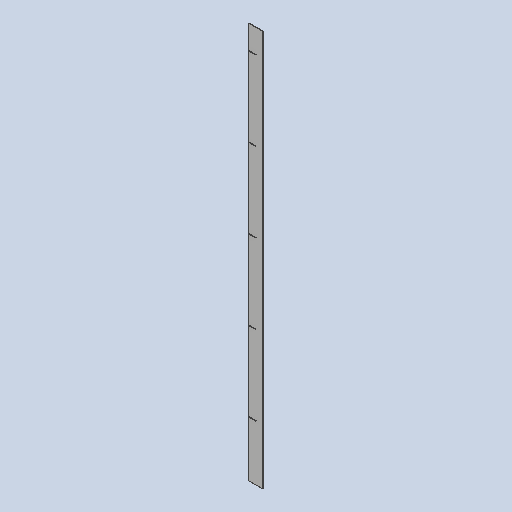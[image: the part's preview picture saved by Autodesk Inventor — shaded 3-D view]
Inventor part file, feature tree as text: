
AUTODESK INVENTOR PART (.ipt)
format: ipt  version: 2025 (Build 290162010, 162A)  size: 148,480 bytes
history: native  units: mm
features: sketch x2, other x2, sheet_metal_op x1, extrude x1, pattern_linear x1, projected_geometry x1
ambient origin geometry x8: Origin, YZ Plane, XZ Plane, XY Plane, X Axis, Y Axis, Z Axis, Center Point
bodies: Body1 (feature_tree)
feature tree (8):
  sheet_metal_op  "Face2"
  extrude  "Extrusion2"  Depth=2500.0mm
  pattern_linear  "Rectangular Pattern1"  Spacing1=46.417287mm  [1 undecoded]
  sketch  "Sketch6"  dims[d26=90.834574mm d27=2500.0mm]
  other  "Plate4"
  sketch  "Sketch7"  dims[d28=3.0mm d29=46.417287mm d30=3.2mm d31=348.4mm d32=0.0mm d33=0.0mm d34=50.0mm d36=500.0mm]
  projected_geometry  "Projected Loop1"
  other  "Definition1"
note: 1 required parameter value undecoded (feature->parameter linkage not recoverable at this tier; creation-order binding heuristic only, values carry confidence <= 0.55)
